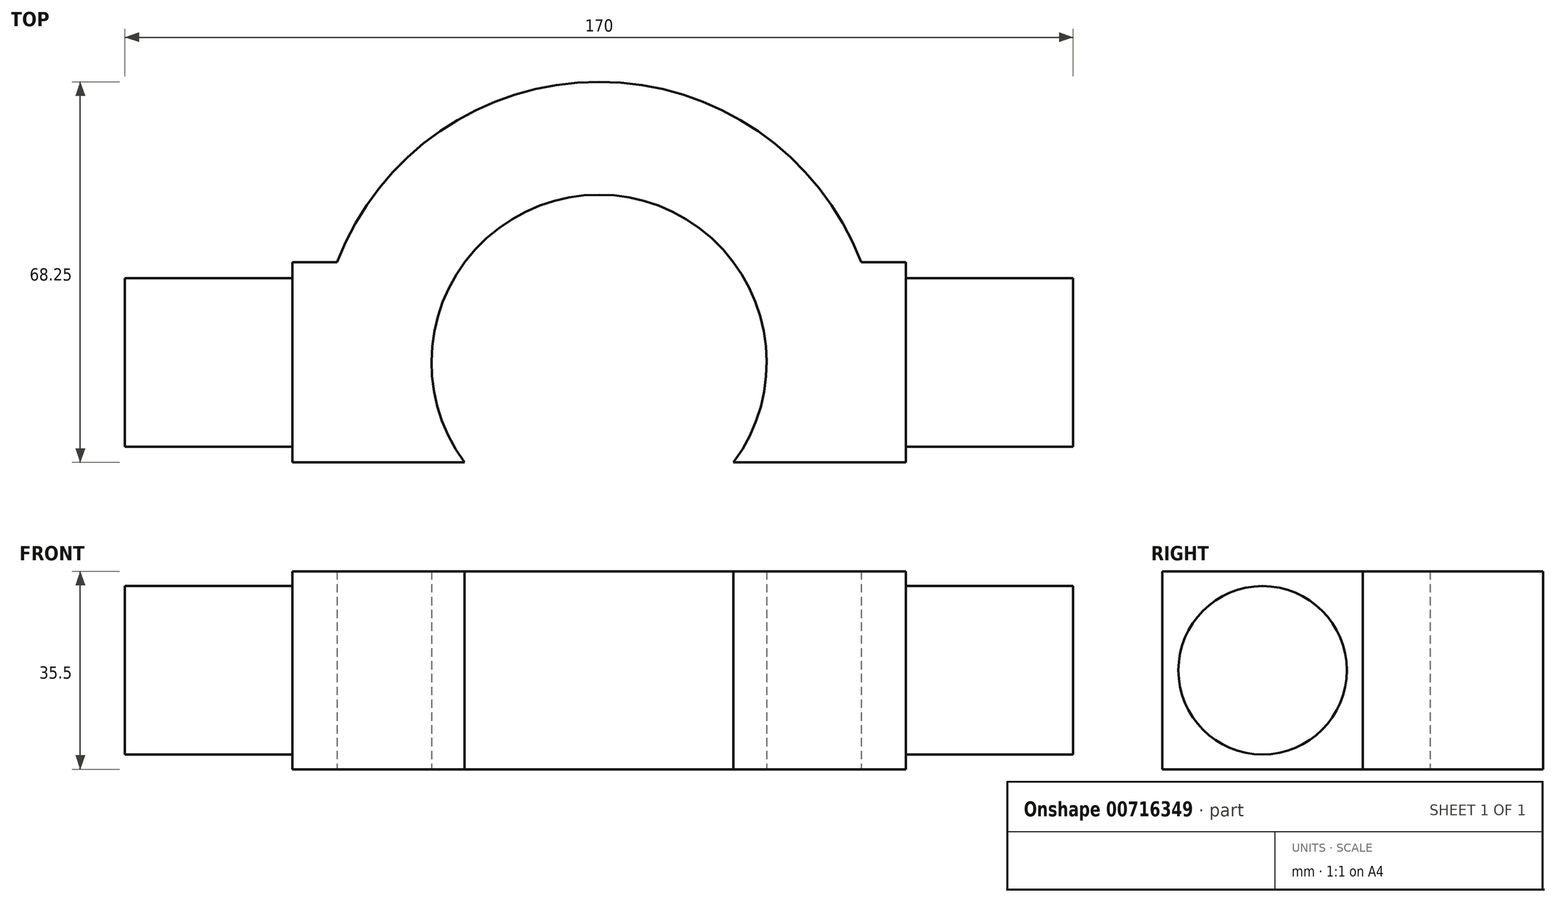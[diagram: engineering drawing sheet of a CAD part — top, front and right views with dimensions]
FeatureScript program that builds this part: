
annotation { "Feature Type Name" : "Feature", "Feature Type Description" : "" }
export const myFeature = defineFeature(function(context is Context, id is Id, definition is map)
    precondition{}
    {
        {
            var Q0;
            Q0=qCreatedBy(makeId("Top.planeOp"),FACE);
            var sketch = newSketch(context, id + "F0", { "sketchPlane" : qUnion([Q0])});
            skCircle(sketch, "E0", {"center": v(0, 0) * mm, "radius": 50.3 * mm});
            skLineSegment(sketch, "E1.bottom", {"start": v(55, 17.95) * mm, "end": v(-55, 17.95) * mm});
            skLineSegment(sketch, "E1.top", {"start": v(55, -17.95) * mm, "end": v(-55, -17.95) * mm});
            skLineSegment(sketch, "E1.left", {"start": v(55, 17.95) * mm, "end": v(55, -17.95) * mm});
            skLineSegment(sketch, "E1.right", {"start": v(-55, 17.95) * mm, "end": v(-55, -17.95) * mm});
            skLineSegment(sketch, "E2", {"start": v(0, 74.96) * mm, "end": v(0, -74.95) * mm, "construction": true});
            skLineSegment(sketch, "E3", {"start": v(-75.23, 0) * mm, "end": v(74.92, 0) * mm, "construction": true});
            skSolve(sketch);
        }
        {
            var Q0;
            {var subQ0=sQuery(id+"F0.wireOp",EDGE,"E1.bottom");var subQ1=sQuery(id+"F0.wireOp",EDGE,"E0");var subQ2=makeQuery(id+"F0.imprint","INTERSECT",VERTEX,{"disambiguationData":[OD(0.0)],"derivedFrom":[subQ1,subQ0]});Q0=makeQuery(id+"F0.imprint","IMPRINT",FACE,{"disambiguationData":[TD([[makeQuery(id+"F0.imprint","IMPRINT",EDGE,{"disambiguationData":[TD([[subQ2,1.0]])],"derivedFrom":subQ1}),1.0]])]});}
            var Q1;
            {var subQ0=sQuery(id+"F0.wireOp",EDGE,"E1.bottom");var subQ1=sQuery(id+"F0.wireOp",EDGE,"E0");var subQ2=makeQuery(id+"F0.imprint","INTERSECT",VERTEX,{"disambiguationData":[OD(0.0)],"derivedFrom":[subQ1,subQ0]});Q1=makeQuery(id+"F0.imprint","IMPRINT",FACE,{"disambiguationData":[TD([[makeQuery(id+"F0.imprint","IMPRINT",EDGE,{"disambiguationData":[TD([[subQ2,-1.0]])],"derivedFrom":subQ1}),1.0]])]});}
            var Q2;
            {var subQ5=sQuery(id+"F0.wireOp",EDGE,"E1.left");Q2=makeQuery(id+"F0.imprint","IMPRINT",FACE,{"disambiguationData":[TD([[makeQuery(id+"F0.imprint","IMPRINT",EDGE,{"derivedFrom":subQ5}),-1.0]])]});}
            var Q3;
            {var subQ0=sQuery(id+"F0.wireOp",EDGE,"E1.top");var subQ1=sQuery(id+"F0.wireOp",EDGE,"E0");var subQ2=makeQuery(id+"F0.imprint","INTERSECT",VERTEX,{"disambiguationData":[OD(0.0)],"derivedFrom":[subQ1,subQ0]});Q3=makeQuery(id+"F0.imprint","IMPRINT",FACE,{"disambiguationData":[TD([[makeQuery(id+"F0.imprint","IMPRINT",EDGE,{"disambiguationData":[TD([[subQ2,-1.0]])],"derivedFrom":subQ1}),1.0]])]});}
            var Q4;
            {var subQ5=sQuery(id+"F0.wireOp",EDGE,"E1.right");Q4=makeQuery(id+"F0.imprint","IMPRINT",FACE,{"disambiguationData":[TD([[makeQuery(id+"F0.imprint","IMPRINT",EDGE,{"derivedFrom":subQ5}),1.0]])]});}
            extrude(context, id + "F1", {"entities" : qUnion([Q0, Q1, Q2, Q3, Q4]), "flatOperationType" : FlatOperationType.REMOVE, "endBound" : BoundingType.SYMMETRIC, "depth" : 35.5 * mm, "offsetDistance" : 25 * mm, "domain" : OperationDomain.MODEL});
        }
        {
            var Q0;
            Q0=makeQuery(id+"F1.opExtrude","SWEPT_FACE",FACE,{"disambiguationData":[OSD([sQuery(id+"F0.wireOp",EDGE,"E1.left")])]});
            cPlane(context, id + "F2", {"entities" : qUnion([Q0]), "cplaneType" : CPlaneType.OFFSET, "offset" : 0 * mm, "width" : 150 * mm, "height" : 150 * mm});
        }
        {
            var Q0;
            Q0=qCreatedBy(id+"F2.planeOp",FACE);
            var sketch = newSketch(context, id + "F3", { "sketchPlane" : qUnion([Q0])});
            skCircle(sketch, "E4", {"center": v(0, 0) * mm, "radius": 15.1 * mm});
            skSolve(sketch);
        }
        {
            var Q0;
            Q0 = qSketchRegion(id + "F3", true);
            extrude(context, id + "F4", {"entities" : qUnion([Q0]), "operationType" : NewBodyOperationType.ADD, "depth" : 30 * mm, "offsetDistance" : 25 * mm});
        }
        {
            var Q0;
            Q0=makeQuery(id+"F1.opExtrude","SWEPT_FACE",FACE,{"disambiguationData":[OSD([sQuery(id+"F0.wireOp",EDGE,"E1.right")])]});
            cPlane(context, id + "F5", {"entities" : qUnion([Q0]), "cplaneType" : CPlaneType.OFFSET, "offset" : 0 * mm, "width" : 150 * mm, "height" : 150 * mm});
        }
        {
            var Q0;
            Q0=qCreatedBy(id+"F5.planeOp",FACE);
            var sketch = newSketch(context, id + "F6", { "sketchPlane" : qUnion([Q0])});
            skCircle(sketch, "E5", {"center": v(0, 0) * mm, "radius": 15.1 * mm});
            skSolve(sketch);
        }
        {
            var Q0;
            Q0 = qSketchRegion(id + "F6", true);
            extrude(context, id + "F7", {"entities" : qUnion([Q0]), "operationType" : NewBodyOperationType.ADD, "depth" : 30 * mm, "offsetDistance" : 25 * mm});
        }
        {
            var Q0;
            Q0=makeQuery(id+"F1.opExtrude","CAP_FACE",FACE,{"disambiguationData":[OSD([sQuery(id+"F0.wireOp",EDGE,"E0"),sQuery(id+"F0.wireOp",EDGE,"E1.bottom"),sQuery(id+"F0.wireOp",EDGE,"E1.top"),sQuery(id+"F0.wireOp",EDGE,"E1.left"),sQuery(id+"F0.wireOp",EDGE,"E1.right")])],"isStart":true});
            cPlane(context, id + "F8", {"entities" : qUnion([Q0]), "cplaneType" : CPlaneType.OFFSET, "offset" : 0 * mm, "width" : 150 * mm, "height" : 150 * mm});
        }
        {
            var Q0;
            Q0=qCreatedBy(id+"F8.planeOp",FACE);
            var sketch = newSketch(context, id + "F9", { "sketchPlane" : qUnion([Q0])});
            skPoint(sketch, "E6", {"position": v(0, 0) * mm});
            skSolve(sketch);
        }
        {
            var Q0;
            Q0=sQuery(id+"F9.wireOp",VERTEX,"E6");
            var Q1;
            Q1=makeQuery(id+"F1.opExtrude","SWEPT_BODY",BODY,{"disambiguationData":[OSD([sQuery(id+"F0.wireOp",EDGE,"E0"),sQuery(id+"F0.wireOp",EDGE,"E1.bottom"),sQuery(id+"F0.wireOp",EDGE,"E1.top"),sQuery(id+"F0.wireOp",EDGE,"E1.left"),sQuery(id+"F0.wireOp",EDGE,"E1.right")])]});
            hole(context, id + "F10", {"style" : HoleStyle.SIMPLE, "endStyle" : HoleEndStyle.THROUGH, "holeDiameter" : 60.1 * mm, "majorDiameter" : 5 * mm, "isTappedThrough" : true, "tappedDepth" : 12 * mm, "tapClearance" : 3, "locations" : qUnion([Q0]), "scope" : qUnion([Q1])});
        }
    });
